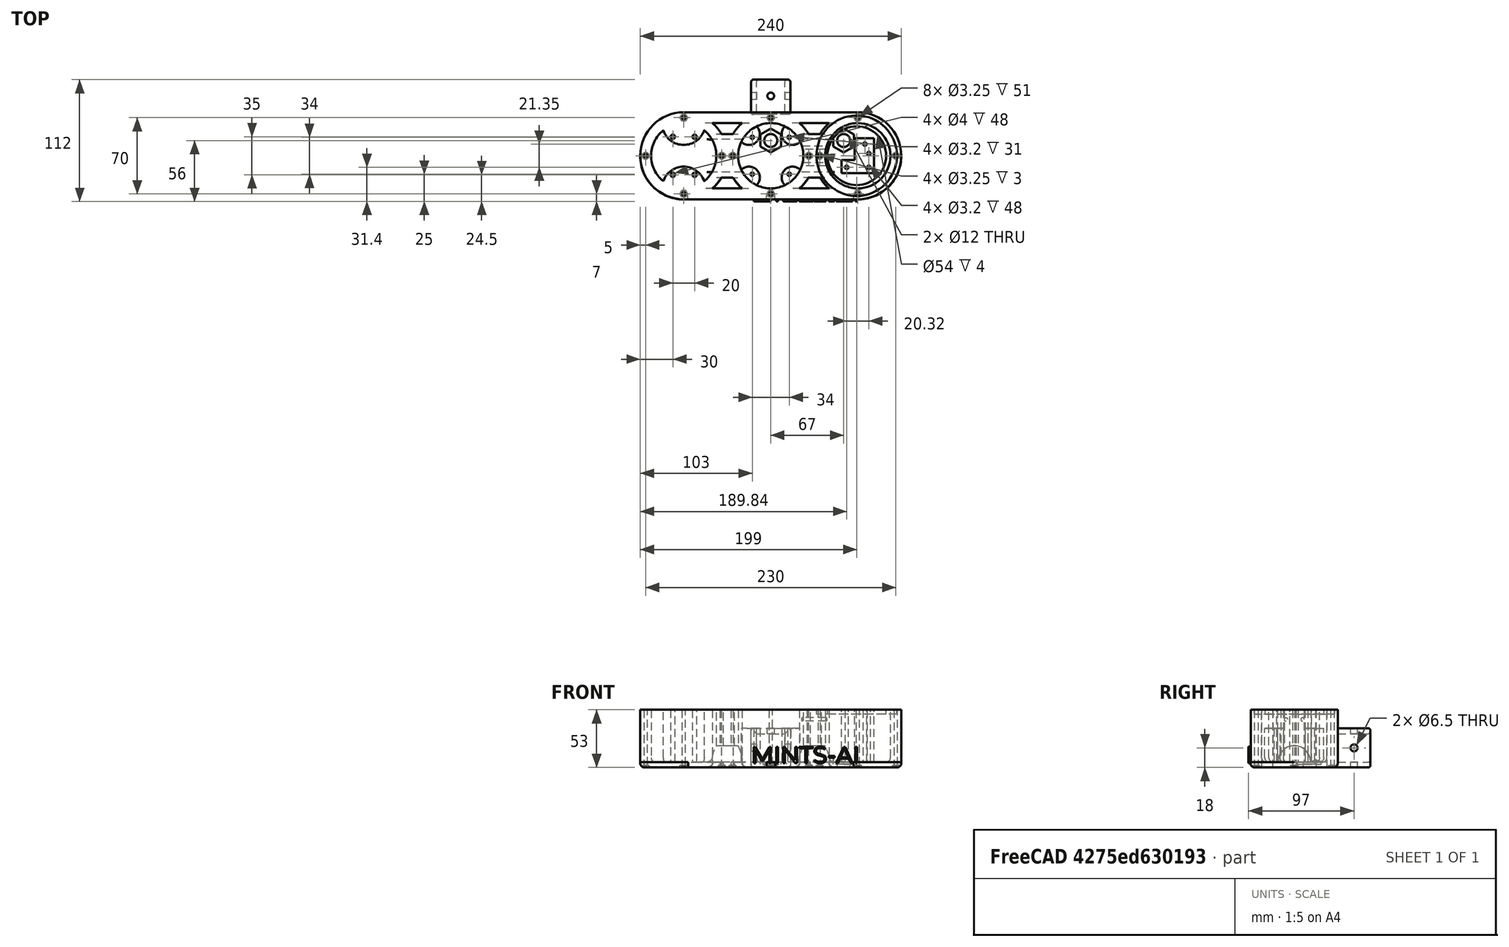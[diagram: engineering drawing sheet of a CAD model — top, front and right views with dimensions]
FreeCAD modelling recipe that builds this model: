
FCSTD DOCUMENT  (FreeCAD 1.0R39319 (Git))
Label: newLight
License: All rights reserved
LicenseURL: https://en.wikipedia.org/wiki/All_rights_reserved
objects: Part::MultiFuse×34, Part::FeaturePython×26, Part::Extrusion×18, Sketcher::SketchObject×17, Part::Cylinder×13, Part::Fillet×6, Part::Cut×3, Part::Part2DObjectPython×1
note: 135 computed .brp shape members not serialized (recipe doc carries the construction recipe); baked Part::Feature solids carry a one-line shape summary decoded from their .brp

FEATURE [Part::FeaturePython] Clone054  label="M3Nut076"  # WARN: FeaturePython — macro-defined, semantics opaque (R4)
  AttacherType = Attacher::AttachEngine3D
  Fuse = false
  Placement = pos=(0,0,4.5) rot=(0,0,1;0rad)
  Scale = (1.1,1.1,5)
FEATURE [Part::FeaturePython] Clone055  label="M3Nut077"  # WARN: FeaturePython — macro-defined, semantics opaque (R4)
  AttacherType = Attacher::AttachEngine3D
  Fuse = false
  Placement = pos=(0,0,0.9) rot=(0,0,1;0rad)
  Scale = (1.1,1.1,1)
FEATURE [Part::FeaturePython] Clone056  label="M3Nut078"  # WARN: FeaturePython — macro-defined, semantics opaque (R4)
  AttacherType = Attacher::AttachEngine3D
  Fuse = false
  Placement = pos=(0,0,4.5) rot=(0,0,1;0rad)
  Scale = (1.1,1.1,5)
FEATURE [Part::FeaturePython] Clone057  label="M3Nut079"  # WARN: FeaturePython — macro-defined, semantics opaque (R4)
  AttacherType = Attacher::AttachEngine3D
  Fuse = false
  Placement = pos=(0,0,0.9) rot=(0,0,1;0rad)
  Scale = (1.1,1.1,1)
FEATURE [Part::FeaturePython] Clone058  label="M3Nut080"  # WARN: FeaturePython — macro-defined, semantics opaque (R4)
  AttacherType = Attacher::AttachEngine3D
  Fuse = false
  Placement = pos=(0,0,4.5) rot=(0,0,1;0rad)
  Scale = (1.1,1.1,5)
FEATURE [Part::FeaturePython] Clone059  label="M3Nut081"  # WARN: FeaturePython — macro-defined, semantics opaque (R4)
  AttacherType = Attacher::AttachEngine3D
  Fuse = false
  Placement = pos=(0,0,0.9) rot=(0,0,1;0rad)
  Scale = (1.1,1.1,1)
FEATURE [Part::FeaturePython] Clone060  label="M3Nut082"  # WARN: FeaturePython — macro-defined, semantics opaque (R4)
  AttacherType = Attacher::AttachEngine3D
  Fuse = false
  Placement = pos=(0,0,4.5) rot=(0,0,1;0rad)
  Scale = (1.1,1.1,5)
FEATURE [Part::FeaturePython] Clone061  label="M3Nut083"  # WARN: FeaturePython — macro-defined, semantics opaque (R4)
  AttacherType = Attacher::AttachEngine3D
  Fuse = false
  Placement = pos=(0,0,0.9) rot=(0,0,1;0rad)
  Scale = (1.1,1.1,1)
FEATURE [Part::FeaturePython] Clone062  label="M3Nut084"  # WARN: FeaturePython — macro-defined, semantics opaque (R4)
  AttacherType = Attacher::AttachEngine3D
  Fuse = false
  Placement = pos=(0,0,4.5) rot=(0,0,1;0rad)
  Scale = (1.1,1.1,5)
FEATURE [Part::FeaturePython] Clone063  label="M3Nut085"  # WARN: FeaturePython — macro-defined, semantics opaque (R4)
  AttacherType = Attacher::AttachEngine3D
  Fuse = false
  Placement = pos=(0,0,0.9) rot=(0,0,1;0rad)
  Scale = (1.1,1.1,1)
FEATURE [Part::FeaturePython] Clone064  label="M3Nut086"  # WARN: FeaturePython — macro-defined, semantics opaque (R4)
  AttacherType = Attacher::AttachEngine3D
  Fuse = false
  Placement = pos=(0,0,4.5) rot=(0,0,1;0rad)
  Scale = (1.1,1.1,5)
FEATURE [Part::FeaturePython] Clone065  label="M3Nut087"  # WARN: FeaturePython — macro-defined, semantics opaque (R4)
  AttacherType = Attacher::AttachEngine3D
  Fuse = false
  Placement = pos=(0,0,0.9) rot=(0,0,1;0rad)
  Scale = (1.1,1.1,1)
FEATURE [Part::FeaturePython] Clone066  label="M3Nut088"  # WARN: FeaturePython — macro-defined, semantics opaque (R4)
  AttacherType = Attacher::AttachEngine3D
  Fuse = false
  Placement = pos=(0,0,4.5) rot=(0,0,1;0rad)
  Scale = (1.1,1.1,5)
FEATURE [Part::FeaturePython] Clone067  label="M3Nut089"  # WARN: FeaturePython — macro-defined, semantics opaque (R4)
  AttacherType = Attacher::AttachEngine3D
  Fuse = false
  Placement = pos=(0,0,0.9) rot=(0,0,1;0rad)
  Scale = (1.1,1.1,1)
FEATURE [Part::FeaturePython] Clone068  label="M3Nut090"  # WARN: FeaturePython — macro-defined, semantics opaque (R4)
  AttacherType = Attacher::AttachEngine3D
  Fuse = false
  Placement = pos=(0,0,4.5) rot=(0,0,1;0rad)
  Scale = (1.1,1.1,5)
FEATURE [Part::FeaturePython] Clone069  label="M3Nut091"  # WARN: FeaturePython — macro-defined, semantics opaque (R4)
  AttacherType = Attacher::AttachEngine3D
  Fuse = false
  Placement = pos=(0,0,0.9) rot=(0,0,1;0rad)
  Scale = (1.1,1.1,1)
FEATURE [Part::FeaturePython] Clone070  label="M3Nut092"  # WARN: FeaturePython — macro-defined, semantics opaque (R4)
  AttacherType = Attacher::AttachEngine3D
  Fuse = false
  Placement = pos=(0,0,4.5) rot=(0,0,1;0rad)
  Scale = (1.1,1.1,5)
FEATURE [Part::FeaturePython] Clone071  label="M3Nut093"  # WARN: FeaturePython — macro-defined, semantics opaque (R4)
  AttacherType = Attacher::AttachEngine3D
  Fuse = false
  Placement = pos=(0,0,0.9) rot=(0,0,1;0rad)
  Scale = (1.1,1.1,1)
FEATURE [Part::FeaturePython] Clone072  label="M3Nut094"  # WARN: FeaturePython — macro-defined, semantics opaque (R4)
  AttacherType = Attacher::AttachEngine3D
  Fuse = false
  Placement = pos=(0,0,4.5) rot=(0,0,1;0rad)
  Scale = (1.1,1.1,5)
FEATURE [Part::FeaturePython] Clone073  label="M3Nut095"  # WARN: FeaturePython — macro-defined, semantics opaque (R4)
  AttacherType = Attacher::AttachEngine3D
  Fuse = false
  Placement = pos=(0,0,0.9) rot=(0,0,1;0rad)
  Scale = (1.1,1.1,1)
FEATURE [Part::FeaturePython] Clone074  label="M3Nut096"  # WARN: FeaturePython — macro-defined, semantics opaque (R4)
  AttacherType = Attacher::AttachEngine3D
  Fuse = false
  Placement = pos=(0,0,4.5) rot=(0,0,1;0rad)
  Scale = (1.1,1.1,5)
FEATURE [Part::FeaturePython] Clone075  label="M3Nut097"  # WARN: FeaturePython — macro-defined, semantics opaque (R4)
  AttacherType = Attacher::AttachEngine3D
  Fuse = false
  Placement = pos=(0,0,0.9) rot=(0,0,1;0rad)
  Scale = (1.1,1.1,1)
FEATURE [Part::FeaturePython] Clone076  label="M3Nut098"  # WARN: FeaturePython — macro-defined, semantics opaque (R4)
  AttacherType = Attacher::AttachEngine3D
  Fuse = false
  Placement = pos=(0,0,4.5) rot=(0,0,1;0rad)
  Scale = (1.1,1.1,5)
FEATURE [Part::FeaturePython] Clone077  label="M3Nut099"  # WARN: FeaturePython — macro-defined, semantics opaque (R4)
  AttacherType = Attacher::AttachEngine3D
  Fuse = false
  Placement = pos=(0,0,0.9) rot=(0,0,1;0rad)
  Scale = (1.1,1.1,1)
FEATURE [Part::FeaturePython] Clone078  label="M3Nut100"  # WARN: FeaturePython — macro-defined, semantics opaque (R4)
  AttacherType = Attacher::AttachEngine3D
  Fuse = false
  Placement = pos=(0,0,4.5) rot=(0,0,1;0rad)
  Scale = (1.1,1.1,5)
FEATURE [Part::FeaturePython] Clone079  label="M3Nut101"  # WARN: FeaturePython — macro-defined, semantics opaque (R4)
  AttacherType = Attacher::AttachEngine3D
  Fuse = false
  Placement = pos=(0,0,0.9) rot=(0,0,1;0rad)
  Scale = (1.1,1.1,1)
FEATURE [Part::Cylinder] Cylinder207 .. Cylinder219  x13 (patterned run collapsed; names and placements below)
  Angle = 360
  AttacherType = Attacher::AttachEngine3D
  FirstAngle = 0
  Height = 9
  Radius = 2
  SecondAngle = 0
FEATURE [Part::MultiFuse] Fusion265
  Shapes = -> [Clone054,Cylinder207]
FEATURE [Part::MultiFuse] Fusion266  label="m3NutCut027"
  Placement = pos=(-80,-235,-22.5) rot=(0.707107,-0.707107,0;3.14159rad)
  Shapes = -> [Clone055,Fusion265]
FEATURE [Part::MultiFuse] Fusion267
  Shapes = -> [Clone056,Cylinder208]
FEATURE [Part::MultiFuse] Fusion268  label="m3NutCut028"
  Placement = pos=(-115,-270,-22.5) rot=(1,0,0;3.14159rad)
  Shapes = -> [Clone057,Fusion267]
FEATURE [Part::MultiFuse] Fusion269
  Shapes = -> [Clone058,Cylinder209]
FEATURE [Part::MultiFuse] Fusion270  label="m3NutCut029"
  Placement = pos=(-45,-270,-22.5) rot=(1,0,0;3.14159rad)
  Shapes = -> [Clone059,Fusion269]
FEATURE [Part::MultiFuse] Fusion271
  Shapes = -> [Clone060,Cylinder210]
FEATURE [Part::MultiFuse] Fusion272  label="m3NutCut030"
  Placement = pos=(-35,-270,-22.5) rot=(1,0,0;3.14159rad)
  Shapes = -> [Clone061,Fusion271]
FEATURE [Part::MultiFuse] Fusion273
  Shapes = -> [Clone062,Cylinder211]
FEATURE [Part::MultiFuse] Fusion274  label="m3NutCut031"
  Placement = pos=(35,-270,-22.5) rot=(1,0,0;3.14159rad)
  Shapes = -> [Clone063,Fusion273]
FEATURE [Part::MultiFuse] Fusion275
  Shapes = -> [Clone064,Cylinder212]
FEATURE [Part::MultiFuse] Fusion276  label="m3NutCut032"
  Placement = pos=(45,-270,-22.5) rot=(1,0,0;3.14159rad)
  Shapes = -> [Clone065,Fusion275]
FEATURE [Part::MultiFuse] Fusion277
  Shapes = -> [Clone066,Cylinder213]
FEATURE [Part::MultiFuse] Fusion278  label="m3NutCut033"
  Placement = pos=(115,-270,-22.5) rot=(1,0,0;3.14159rad)
  Shapes = -> [Clone067,Fusion277]
FEATURE [Part::MultiFuse] Fusion279
  Shapes = -> [Clone068,Cylinder214]
FEATURE [Part::MultiFuse] Fusion280  label="m3NutCut034"
  Placement = pos=(-80,-235,-22.5) rot=(0.707107,-0.707107,0;3.14159rad)
  Shapes = -> [Clone069,Fusion279]
FEATURE [Part::MultiFuse] Fusion281
  Shapes = -> [Clone070,Cylinder215]
FEATURE [Part::MultiFuse] Fusion282  label="m3NutCut035"
  Placement = pos=(0,-235,-22.5) rot=(0.707107,-0.707107,0;3.14159rad)
  Shapes = -> [Clone071,Fusion281]
FEATURE [Part::MultiFuse] Fusion283
  Shapes = -> [Clone072,Cylinder216]
FEATURE [Part::MultiFuse] Fusion284  label="m3NutCut036"
  Placement = pos=(80,-235,-22.5) rot=(0.707107,-0.707107,0;3.14159rad)
  Shapes = -> [Clone073,Fusion283]
FEATURE [Part::MultiFuse] Fusion285
  Shapes = -> [Clone074,Cylinder217]
FEATURE [Part::MultiFuse] Fusion286  label="m3NutCut037"
  Placement = pos=(80,-305,-22.5) rot=(0.707107,-0.707107,0;3.14159rad)
  Shapes = -> [Clone075,Fusion285]
FEATURE [Part::MultiFuse] Fusion287
  Shapes = -> [Clone076,Cylinder218]
FEATURE [Part::MultiFuse] Fusion288  label="m3NutCut038"
  Placement = pos=(1.4e-14,-305,-22.5) rot=(0.707107,-0.707107,0;3.14159rad)
  Shapes = -> [Clone077,Fusion287]
FEATURE [Part::MultiFuse] Fusion289
  Shapes = -> [Clone078,Cylinder219]
FEATURE [Part::MultiFuse] Fusion290  label="m3NutCut039"
  Placement = pos=(-80,-305,-22.5) rot=(0.707107,-0.707107,0;3.14159rad)
  Shapes = -> [Clone079,Fusion289]
FEATURE [Part::MultiFuse] Fusion291  label="m3NutCuts001"
  Placement = pos=(0,0,-0.5) rot=(0,0,1;0rad)
  Shapes = -> [Fusion266,Fusion268,Fusion270,Fusion272,Fusion274,Fusion276,Fusion278,Fusion280,Fusion282,Fusion284,Fusion286,Fusion288,Fusion290]
FEATURE [Part::Part2DObjectPython] ShapeString002  # Draft 2D object (typed FeaturePython)
  FontFile = <userpath>/Downloads/Montserrat-Regular.otf
  Fuse = false
  Justification = 6
  JustificationReference = 0
  KeepLeftMargin = false
  MakeFace = true
  ObliqueAngle = 0
  Placement = pos=(-15.5,-310,-21) rot=(1,0,0;1.5708rad)
  ScaleToSize = true
  Size = 15
  String = MINTS-AI
  Tracking = 0
FEATURE [Part::Extrusion] Extrude191  label="text001"
  Base = -> ShapeString002
  Dir = (0,-1,2e-16)
  DirMode = 2
  FaceMakerClass = Part::FaceMakerBullseye
  FaceMakerMode = 3
  LengthFwd = 2
  LengthRev = 0
  Solid = false
  Symmetric = false
FEATURE [Sketcher::SketchObject] Sketch409
  ArcFitTolerance = 0
  FullyConstrained = true
  MakeInternals = false
  Placement = pos=(0,0,-25) rot=(0,0,1;0rad)
  sketch-geometry (12):
    g0: Circle CenterX=-115 CenterY=-270 CenterZ=0 NormalX=0 NormalY=0 NormalZ=1 AngleXU=0 Radius=1.625
    g1: Circle CenterX=-80 CenterY=-235 CenterZ=0 NormalX=0 NormalY=0 NormalZ=1 AngleXU=0 Radius=1.625
    g2: Circle CenterX=-80 CenterY=-305 CenterZ=0 NormalX=0 NormalY=0 NormalZ=1 AngleXU=0 Radius=1.625
    g3: Circle CenterX=-45 CenterY=-270 CenterZ=0 NormalX=0 NormalY=0 NormalZ=1 AngleXU=0 Radius=1.625
    g4: Circle CenterX=-35 CenterY=-270 CenterZ=0 NormalX=0 NormalY=0 NormalZ=1 AngleXU=0 Radius=1.625
    g5: Circle CenterX=0 CenterY=-305 CenterZ=0 NormalX=0 NormalY=0 NormalZ=1 AngleXU=0 Radius=1.625
    g6: Circle CenterX=0 CenterY=-235 CenterZ=0 NormalX=0 NormalY=0 NormalZ=1 AngleXU=0 Radius=1.625
    g7: Circle CenterX=35 CenterY=-270 CenterZ=0 NormalX=0 NormalY=0 NormalZ=1 AngleXU=0 Radius=1.625
    g8: Circle CenterX=45 CenterY=-270 CenterZ=0 NormalX=0 NormalY=0 NormalZ=1 AngleXU=0 Radius=1.625
    g9: Circle CenterX=80 CenterY=-235 CenterZ=0 NormalX=0 NormalY=0 NormalZ=1 AngleXU=0 Radius=1.625
    g10: Circle CenterX=115 CenterY=-270 CenterZ=0 NormalX=0 NormalY=0 NormalZ=1 AngleXU=0 Radius=1.625
    g11: Circle CenterX=80 CenterY=-305 CenterZ=0 NormalX=0 NormalY=0 NormalZ=1 AngleXU=0 Radius=1.625
  constraints (36):
    c: PointOnObject(g5,g-2)
    c: PointOnObject(g6,g-2)
    c: Equal(g8,g1)
    c: Equal(g8,g6)
    c: Equal(g8,g9)
    c: Equal(g8,g2)
    c: Equal(g8,g5)
    c: Equal(g8,g11)
    c: Equal(g8,g0)
    c: Equal(g8,g3)
    c: Equal(g8,g4)
    c: Equal(g8,g7)
    c: Equal(g8,g10)
    c: Diameter(g8) = 3.25
    c: Horizontal(g0,g3)
    c: Horizontal(g3,g4)
    c: Horizontal(g4,g7)
    c: Horizontal(g7,g8)
    c: Horizontal(g8,g10)
    c: Horizontal(g2,g5)
    c: Horizontal(g5,g11)
    c: Horizontal(g6,g9)
    c: Horizontal(g1,g6)
    c: Vertical(g2,g1)
    c: Vertical(g9,g11)
    c: DistanceY(g0) = -270
    c: DistanceX(g0) = -115
    c: DistanceX(g0,g2) = 35
    c: DistanceY(g2,g0) = 35
    c: DistanceY(g0,g1) = 35
    c: DistanceX(g0,g3) = 70
    c: DistanceX(g4) = -35
    c: DistanceX(g7) = 35
    c: DistanceX(g8) = 45
    c: DistanceX(g8,g10) = 70
    c: DistanceX(g8,g11) = 35
FEATURE [Part::Extrusion] Extrude184  label="m3Cuts001"
  Base = -> Sketch409
  Dir = (0,0,1)
  DirMode = 2
  FaceMakerClass = Part::FaceMakerBullseye
  FaceMakerMode = 3
  LengthFwd = 60
  LengthRev = 0
  Solid = true
  Symmetric = false
FEATURE [Sketcher::SketchObject] Sketch410
  ArcFitTolerance = 0
  FullyConstrained = true
  MakeInternals = false
  Placement = pos=(24,0,0) rot=(0.57735,0.57735,0.57735;2.0944rad)
  sketch-geometry (2):
    g0: Circle CenterX=-277.6 CenterY=19.15 CenterZ=0 NormalX=0 NormalY=0 NormalZ=1 AngleXU=0 Radius=1.6
    g1: Circle CenterX=-262.4 CenterY=19.15 CenterZ=0 NormalX=0 NormalY=0 NormalZ=1 AngleXU=0 Radius=1.6
  constraints (6):
    c: Horizontal(g1,g0)
    c: Equal(g1,g0)
    c: Diameter(g1) = 3.2
    c: DistanceX(g0) = -277.6
    c: DistanceY(g0) = 19.15
    c: DistanceX(g0,g1) = 15.2
FEATURE [Part::Extrusion] Extrude185
  Base = -> Sketch410
  Dir = (1,0,0)
  DirMode = 2
  FaceMakerClass = Part::FaceMakerBullseye
  FaceMakerMode = 3
  LengthFwd = 30
  LengthRev = 0
  Solid = true
  Symmetric = false
FEATURE [Sketcher::SketchObject] Sketch411
  ArcFitTolerance = 0
  FullyConstrained = true
  MakeInternals = false
  Placement = pos=(0,0,-22) rot=(0,0,1;0rad)
  sketch-geometry (14):
    g0: LineSegment StartX=-2e-16 StartY=-267 StartZ=0 EndX=9.52628 EndY=-261.5 EndZ=0
    g1: LineSegment StartX=9.52628 StartY=-261.5 StartZ=0 EndX=9.52628 EndY=-250.5 EndZ=0
    g2: LineSegment StartX=9.52628 StartY=-250.5 StartZ=0 EndX=2e-16 EndY=-245 EndZ=0
    g3: LineSegment StartX=2e-16 StartY=-245 StartZ=0 EndX=-9.52628 EndY=-250.5 EndZ=0
    g4: LineSegment StartX=-9.52628 StartY=-250.5 StartZ=0 EndX=-9.52628 EndY=-261.5 EndZ=0
    g5: LineSegment StartX=-9.52628 StartY=-261.5 StartZ=0 EndX=-2e-16 EndY=-267 EndZ=0
    g6: Circle [constr] CenterX=2e-16 CenterY=-256 CenterZ=0 NormalX=0 NormalY=0 NormalZ=1 AngleXU=0 Radius=11
    g7: LineSegment StartX=67 StartY=-267 StartZ=0 EndX=76.5263 EndY=-261.5 EndZ=0
    g8: LineSegment StartX=76.5263 StartY=-261.5 StartZ=0 EndX=76.5263 EndY=-250.5 EndZ=0
    g9: LineSegment StartX=76.5263 StartY=-250.5 StartZ=0 EndX=67 EndY=-245 EndZ=0
    g10: LineSegment StartX=67 StartY=-245 StartZ=0 EndX=57.4737 EndY=-250.5 EndZ=0
    g11: LineSegment StartX=57.4737 StartY=-250.5 StartZ=0 EndX=57.4737 EndY=-261.5 EndZ=0
    g12: LineSegment StartX=57.4737 StartY=-261.5 StartZ=0 EndX=67 EndY=-267 EndZ=0
    g13: Circle [constr] CenterX=67 CenterY=-256 CenterZ=0 NormalX=0 NormalY=0 NormalZ=1 AngleXU=0 Radius=11
  constraints (34):
    c: Coincident(g0,g1)
    c: Coincident(g1,g2)
    c: Coincident(g2,g3)
    c: Coincident(g3,g4)
    c: Coincident(g4,g5)
    c: Coincident(g5,g0)
    c: Equal(g0, g1-g5) x5
    c: PointOnObject(g0,g6)
    c: PointOnObject(g1,g6)
    c: PointOnObject(g2,g6)
    c: PointOnObject(g3,g6)
    c: PointOnObject(g4,g6)
    c: PointOnObject(g5,g6)
    c: Coincident(g7,g8)
    c: Coincident(g8,g9)
    c: Coincident(g9,g10)
    c: Coincident(g10,g11)
    c: Coincident(g11,g12)
    c: Coincident(g12,g7)
    c: Equal(g7, g8-g12) x5
    c: PointOnObject(g7,g13)
    c: PointOnObject(g8,g13)
    c: PointOnObject(g9,g13)
    c: PointOnObject(g10,g13)
    c: PointOnObject(g11,g13)
    c: PointOnObject(g12,g13)
    c: Horizontal(g6,g13)
    c: Vertical(g6,g2)
    c: DistanceX(g6) = 0
    c: DistanceY(g6) = -256
    c: Diameter(g6) = 22
    c: Vertical(g13,g7)
    c: Diameter(g13) = 22
    c: DistanceX(g13) = 67
FEATURE [Part::Extrusion] Extrude186
  Base = -> Sketch411
  Dir = (0,0,1)
  DirMode = 2
  FaceMakerClass = Part::FaceMakerBullseye
  FaceMakerMode = 3
  LengthFwd = 6
  LengthRev = 0
  Solid = true
  Symmetric = false
FEATURE [Part::MultiFuse] Fusion293  label="pg7Cuts001"
  Shapes = -> [Extrude185,Extrude186]
FEATURE [Sketcher::SketchObject] Sketch412
  ArcFitTolerance = 0
  FullyConstrained = true
  MakeInternals = false
  Placement = pos=(0,-232,0) rot=(1,0,0;1.5708rad)
  sketch-geometry (8):
    g0: LineSegment StartX=-13 StartY=6 StartZ=0 EndX=13 EndY=6 EndZ=0
    g1: LineSegment StartX=13 StartY=6 StartZ=0 EndX=13 EndY=-20 EndZ=0
    g2: LineSegment StartX=13 StartY=-20 StartZ=0 EndX=-13 EndY=-20 EndZ=0
    g3: LineSegment StartX=-13 StartY=-20 StartZ=0 EndX=-13 EndY=6 EndZ=0
    g4: LineSegment StartX=-18 StartY=11 StartZ=0 EndX=18 EndY=11 EndZ=0
    g5: LineSegment StartX=18 StartY=11 StartZ=0 EndX=18 EndY=-25 EndZ=0
    g6: LineSegment StartX=18 StartY=-25 StartZ=0 EndX=-18 EndY=-25 EndZ=0
    g7: LineSegment StartX=-18 StartY=-25 StartZ=0 EndX=-18 EndY=11 EndZ=0
  constraints (24):
    c: Coincident(g0,g1)
    c: Coincident(g1,g2)
    c: Coincident(g2,g3)
    c: Coincident(g3,g0)
    c: Horizontal(g0)
    c: Horizontal(g2)
    c: Vertical(g1)
    c: Vertical(g3)
    c: Coincident(g4,g5)
    c: Coincident(g5,g6)
    c: Coincident(g6,g7)
    c: Coincident(g7,g4)
    c: Horizontal(g4)
    c: Horizontal(g6)
    c: Vertical(g5)
    c: Vertical(g7)
    c: DistanceY(g6) = -25
    c: DistanceX(g2,g1) = 26
    c: DistanceX(g6) = -18
    c: DistanceX(g6,g2) = 5
    c: DistanceX(g5) = 18
    c: DistanceY(g2,g0) = 26
    c: DistanceY(g6,g2) = 5
    c: DistanceY(g0,g4) = 5
FEATURE [Part::Extrusion] Extrude187
  Base = -> Sketch412
  Dir = (0,-1,2e-16)
  DirMode = 2
  FaceMakerClass = Part::FaceMakerBullseye
  FaceMakerMode = 3
  LengthFwd = 32
  LengthRev = 0
  Reversed = true
  Solid = true
  Symmetric = false
FEATURE [Sketcher::SketchObject] Sketch413
  ArcFitTolerance = 0
  FullyConstrained = true
  MakeInternals = false
  Placement = pos=(0,0,11) rot=(0,0,1;0rad)
  sketch-geometry (1):
    g0: Circle CenterX=0 CenterY=-215 CenterZ=0 NormalX=0 NormalY=0 NormalZ=1 AngleXU=0 Radius=3.125
  constraints (3):
    c: DistanceX(g0) = 0
    c: DistanceY(g0) = -215
    c: Diameter(g0) = 6.25
FEATURE [Part::Extrusion] Extrude189
  Base = -> Sketch413
  Dir = (0,0,1)
  DirMode = 2
  FaceMakerClass = Part::FaceMakerBullseye
  FaceMakerMode = 3
  LengthFwd = 36
  LengthRev = 0
  Reversed = true
  Solid = true
  Symmetric = false
FEATURE [Sketcher::SketchObject] Sketch414
  ArcFitTolerance = 0
  FullyConstrained = true
  MakeInternals = false
  Placement = pos=(-18,0,0) rot=(0.57735,0.57735,0.57735;2.0944rad)
  sketch-geometry (1):
    g0: Circle CenterX=-215 CenterY=-7 CenterZ=0 NormalX=0 NormalY=0 NormalZ=1 AngleXU=0 Radius=3.25
  constraints (3):
    c: DistanceX(g0) = -215
    c: DistanceY(g0) = -7
    c: Diameter(g0) = 6.5
FEATURE [Part::Extrusion] Extrude188
  Base = -> Sketch414
  Dir = (1,0,0)
  DirMode = 2
  FaceMakerClass = Part::FaceMakerBullseye
  FaceMakerMode = 3
  LengthFwd = 36
  LengthRev = 0
  Solid = true
  Symmetric = false
FEATURE [Part::MultiFuse] Fusion292
  Shapes = -> [Extrude189,Extrude188]
FEATURE [Part::Cut] Cut158  label="in004"
  Base = -> Extrude187
  Tool = -> Fusion292
FEATURE [Part::Fillet] Fillet262
  Base = -> Cut158
  EdgeLinks = -> Cut158 [?Edge1,?Edge4,?Edge6,?Edge22]
  Edges = 4 edges r=2: [Edge1,Edge4,Edge6,Edge22]
FEATURE [Part::Fillet] Fillet263  label="tSlotHolder001"
  Base = -> Fillet262
  EdgeLinks = -> Fillet262 [Edge4,Edge18,Edge20,Edge21,Edge22,Edge23,Edge24,Edge25,Edge26,Edge27,Edge28,Edge29]
  Edges = 12 edges r=2: [Edge4,Edge18,Edge20,Edge21,Edge22,Edge23,Edge24,Edge25,Edge26,Edge27,Edge28,Edge29]
FEATURE [Sketcher::SketchObject] Sketch415
  ArcFitTolerance = 0
  FullyConstrained = true
  MakeInternals = false
  Placement = pos=(0,0,-25) rot=(0,0,1;0rad)
  sketch-geometry (2):
    g0: Circle CenterX=0 CenterY=-256 CenterZ=0 NormalX=0 NormalY=0 NormalZ=1 AngleXU=0 Radius=6
    g1: Circle CenterX=67 CenterY=-256 CenterZ=0 NormalX=0 NormalY=0 NormalZ=1 AngleXU=0 Radius=6
  constraints (6):
    c: DistanceY(g0) = -256
    c: Horizontal(g0,g1)
    c: DistanceX(g0,g1) = 67
    c: DistanceX(g0) = 0
    c: Equal(g0,g1)
    c: Diameter(g0) = 12
FEATURE [Part::Extrusion] Extrude190  label="outCut001"
  Base = -> Sketch415
  Dir = (0,0,1)
  DirMode = 2
  FaceMakerClass = Part::FaceMakerBullseye
  FaceMakerMode = 3
  LengthFwd = 5
  LengthRev = 0
  Solid = true
  Symmetric = false
FEATURE [Part::MultiFuse] Fusion297  label="mainCuts001"
  Shapes = -> [Fusion293,Fusion291,Extrude190,Extrude184]
FEATURE [Sketcher::SketchObject] Sketch416
  ArcFitTolerance = 0
  FullyConstrained = true
  MakeInternals = false
  Placement = pos=(0,0,-25) rot=(0,0,1;0rad)
  sketch-geometry (8):
    g0: ArcOfCircle CenterX=-80 CenterY=-270 CenterZ=0 NormalX=0 NormalY=0 NormalZ=1 AngleXU=0 Radius=40 StartAngle=1.5708 EndAngle=4.71239
    g1: ArcOfCircle CenterX=80 CenterY=-270 CenterZ=0 NormalX=0 NormalY=0 NormalZ=1 AngleXU=0 Radius=40 StartAngle=4.71239 EndAngle=7.85398
    g2: LineSegment StartX=-80 StartY=-310 StartZ=0 EndX=80 EndY=-310 EndZ=0
    g3: LineSegment StartX=80 StartY=-230 StartZ=0 EndX=-80 EndY=-230 EndZ=0
    g4: ArcOfCircle CenterX=-80 CenterY=-270 CenterZ=0 NormalX=0 NormalY=0 NormalZ=1 AngleXU=0 Radius=30 StartAngle=1.5708 EndAngle=4.71239
    g5: ArcOfCircle CenterX=80 CenterY=-270 CenterZ=0 NormalX=0 NormalY=0 NormalZ=1 AngleXU=0 Radius=30 StartAngle=4.71239 EndAngle=7.85398
    g6: LineSegment StartX=-80 StartY=-300 StartZ=0 EndX=80 EndY=-300 EndZ=0
    g7: LineSegment StartX=80 StartY=-240 StartZ=0 EndX=-80 EndY=-240 EndZ=0
  constraints (18):
    c: Tangent(g0,g2) = -1.5708
    c: Tangent(g2,g1) = -1.5708
    c: Tangent(g1,g3) = -1.5708
    c: Tangent(g3,g0) = -1.5708
    c: Equal(g0,g1)
    c: Horizontal(g2)
    c: DistanceY(g0) = -270
    c: DistanceX(g0) = -80
    c: DistanceX(g1) = 80
    c: Diameter(g0) = 80
    c: Tangent(g4,g6) = -1.5708
    c: Tangent(g6,g5) = -1.5708
    c: Tangent(g5,g7) = -1.5708
    c: Tangent(g7,g4) = -1.5708
    c: Equal(g4,g5)
    c: Coincident(g4,g0)
    c: Coincident(g5,g1)
    c: Diameter(g4) = 60
FEATURE [Part::Extrusion] Extrude192  label="outerBorder002"
  Base = -> Sketch416
  Dir = (0,0,1)
  DirMode = 2
  FaceMakerClass = Part::FaceMakerBullseye
  FaceMakerMode = 3
  LengthFwd = 53
  LengthRev = 0
  Solid = true
  Symmetric = false
FEATURE [Part::Fillet] Fillet264  label="outerHold002"
  Base = -> Extrude192
  EdgeLinks = -> Extrude192 [Edge9]
  Edges = 1 edges r=4: [Edge9]
FEATURE [Sketcher::SketchObject] Sketch417
  ArcFitTolerance = 0
  FullyConstrained = true
  MakeInternals = false
  Placement = pos=(0,0,-25) rot=(0,0,1;0rad)
  sketch-geometry (8):
    g0: ArcOfCircle CenterX=-80 CenterY=-270 CenterZ=0 NormalX=0 NormalY=0 NormalZ=1 AngleXU=0 Radius=30 StartAngle=5.55346 EndAngle=7.01291
    g1: LineSegment StartX=-57.6393 StartY=-250 StartZ=0 EndX=-22.3607 EndY=-250 EndZ=0
    g2: LineSegment StartX=-57.6393 StartY=-290 StartZ=0 EndX=-22.3607 EndY=-290 EndZ=0
    g3: ArcOfCircle CenterX=0 CenterY=-270 CenterZ=0 NormalX=0 NormalY=0 NormalZ=1 AngleXU=0 Radius=30 StartAngle=2.41186 EndAngle=3.87132
    g4: ArcOfCircle CenterX=0 CenterY=-270 CenterZ=0 NormalX=0 NormalY=0 NormalZ=1 AngleXU=0 Radius=30 StartAngle=5.55346 EndAngle=7.01291
    g5: ArcOfCircle CenterX=80 CenterY=-270 CenterZ=0 NormalX=0 NormalY=0 NormalZ=1 AngleXU=0 Radius=30 StartAngle=2.41186 EndAngle=3.87132
    g6: LineSegment StartX=22.3607 StartY=-250 StartZ=0 EndX=57.6393 EndY=-250 EndZ=0
    g7: LineSegment StartX=57.6393 StartY=-290 StartZ=0 EndX=22.3607 EndY=-290 EndZ=0
  constraints (27):
    c: Coincident(g1,g0)
    c: Horizontal(g1)
    c: Coincident(g2,g0)
    c: Horizontal(g2)
    c: PointOnObject(g3,g-2)
    c: Coincident(g3,g2)
    c: Coincident(g3,g1)
    c: Coincident(g4,g3)
    c: Coincident(g6,g4)
    c: Coincident(g6,g5)
    c: Horizontal(g6)
    c: Coincident(g7,g5)
    c: Coincident(g7,g4)
    c: Horizontal(g7)
    c: Horizontal(g0,g4)
    c: Horizontal(g2,g4)
    c: Equal(g3,g0)
    c: Equal(g3,g5)
    c: Equal(g3,g4)
    c: Diameter(g3) = 60
    c: DistanceY(g3) = -270
    c: Vertical(g0,g0)
    c: Vertical(g2,g1)
    c: Vertical(g5,g5)
    c: DistanceX(g5) = 80
    c: DistanceX(g0) = -80
    c: DistanceY(g4) = -250
FEATURE [Part::Extrusion] Extrude193  label="3WayHolds002"
  Base = -> Sketch417
  Dir = (0,0,1)
  DirMode = 2
  FaceMakerClass = Part::FaceMakerBullseye
  FaceMakerMode = 3
  LengthFwd = 53
  LengthRev = 0
  Solid = true
  Symmetric = false
FEATURE [Sketcher::SketchObject] Sketch418
  ArcFitTolerance = 0
  FullyConstrained = true
  MakeInternals = false
  Placement = pos=(0,0,-20) rot=(0,0,1;0rad)
  sketch-geometry (18):
    g0: ArcOfCircle CenterX=-80 CenterY=-240 CenterZ=0 NormalX=0 NormalY=0 NormalZ=1 AngleXU=0 Radius=20 StartAngle=3.48143 EndAngle=5.94335
    g1: ArcOfCircle CenterX=-80 CenterY=-300 CenterZ=0 NormalX=0 NormalY=0 NormalZ=1 AngleXU=0 Radius=20 StartAngle=0.339837 EndAngle=2.80176
    g2: ArcOfCircle CenterX=-80 CenterY=-270 CenterZ=0 NormalX=0 NormalY=0 NormalZ=1 AngleXU=0 Radius=30 StartAngle=0.891123 EndAngle=2.25047
    g3: ArcOfCircle CenterX=-80 CenterY=-270 CenterZ=0 NormalX=0 NormalY=0 NormalZ=1 AngleXU=0 Radius=30 StartAngle=4.03272 EndAngle=5.39206
    g4: LineSegment StartX=65 StartY=-286 StartZ=0 EndX=95 EndY=-286 EndZ=0
    g5: LineSegment StartX=95 StartY=-286 StartZ=0 EndX=95 EndY=-254 EndZ=0
    g6: LineSegment StartX=95 StartY=-254 StartZ=0 EndX=77 EndY=-254 EndZ=0
    g7: LineSegment StartX=77 StartY=-254 StartZ=0 EndX=77 EndY=-274 EndZ=0
    g8: LineSegment StartX=77 StartY=-274 StartZ=0 EndX=65 EndY=-274 EndZ=0
    g9: LineSegment StartX=65 StartY=-274 StartZ=0 EndX=65 EndY=-286 EndZ=0
    g10: Circle CenterX=-90 CenterY=-252.5 CenterZ=0 NormalX=0 NormalY=0 NormalZ=1 AngleXU=0 Radius=2
    g11: Circle CenterX=-70 CenterY=-252.5 CenterZ=0 NormalX=0 NormalY=0 NormalZ=1 AngleXU=0 Radius=2
    g12: Circle CenterX=-90 CenterY=-287.5 CenterZ=0 NormalX=0 NormalY=0 NormalZ=1 AngleXU=0 Radius=2
    g13: Circle CenterX=-70 CenterY=-287.5 CenterZ=0 NormalX=0 NormalY=0 NormalZ=1 AngleXU=0 Radius=2
    g14: Circle CenterX=69.84 CenterY=-280.6 CenterZ=0 NormalX=0 NormalY=0 NormalZ=1 AngleXU=0 Radius=1.6
    g15: Circle CenterX=90.16 CenterY=-280.6 CenterZ=0 NormalX=0 NormalY=0 NormalZ=1 AngleXU=0 Radius=1.6
    g16: Circle CenterX=90.16 CenterY=-267.9 CenterZ=0 NormalX=0 NormalY=0 NormalZ=1 AngleXU=0 Radius=1.6
    g17: Circle CenterX=86.5 CenterY=-259.25 CenterZ=0 NormalX=0 NormalY=0 NormalZ=1 AngleXU=0 Radius=1.6
  constraints (57):
    c: Vertical(g0,g1)
    c: Coincident(g2,g0)
    c: Coincident(g3,g2)
    c: Coincident(g3,g1)
    c: Coincident(g0,g2)
    c: Coincident(g1,g3)
    c: DistanceX(g2) = -80
    c: DistanceY(g2) = -270
    c: Equal(g3,g2)
    c: Diameter(g3) = 60
    c: Equal(g0,g1)
    c: Diameter(g0) = 40
    c: Vertical(g0,g2)
    c: DistanceY(g0) = -240
    c: DistanceY(g1) = -300
    c: Horizontal(g4)
    c: Coincident(g5,g4)
    c: Vertical(g5)
    c: Coincident(g6,g5)
    c: Horizontal(g6)
    c: Coincident(g7,g6)
    c: Vertical(g7)
    c: Coincident(g8,g7)
    c: Horizontal(g8)
    c: Coincident(g9,g8)
    c: Coincident(g9,g4)
    c: Vertical(g9)
    c: DistanceY(g4) = -286
    c: DistanceX(g4) = 65
    c: DistanceY(g4,g8) = 12
    c: DistanceX(g4,g4) = 30
    c: DistanceX(g6,g6) = 18
    c: DistanceY(g5,g5) = 32
    c: Horizontal(g13,g12)
    c: Horizontal(g10,g11)
    c: Vertical(g12,g10)
    c: Vertical(g13,g11)
    c: DistanceX(g12,g2) = 10
    c: DistanceY(g12) = -287.5
    c: DistanceX(g12,g13) = 20
    c: DistanceY(g12,g10) = 35
    c: Equal(g10,g11)
    c: Equal(g10,g13)
    c: Equal(g10,g12)
    c: Diameter(g10) = 4
    c: Horizontal(g14,g15)
    c: Vertical(g15,g16)
    c: DistanceX(g14,g15) = 20.32
    c: DistanceY(g14) = -280.6
    c: DistanceY(g15,g16) = 12.7
    c: DistanceX(g17,g16) = 3.66
    c: DistanceY(g16,g17) = 8.65
    c: Equal(g15,g16)
    c: Equal(g15,g17)
    c: Equal(g15,g14)
    c: Diameter(g15) = 3.2
    c: DistanceX(g4,g14) = 4.84
FEATURE [Part::Extrusion] Extrude194  label="i2cHolds002"
  Base = -> Sketch418
  Dir = (0,0,1)
  DirMode = 2
  FaceMakerClass = Part::FaceMakerBullseye
  FaceMakerMode = 3
  LengthFwd = 48
  LengthRev = 0
  Solid = true
  Symmetric = false
FEATURE [Sketcher::SketchObject] Sketch419
  ArcFitTolerance = 0
  FullyConstrained = true
  MakeInternals = false
  Placement = pos=(0,0,-20) rot=(0,0,1;0rad)
  sketch-geometry (12):
    g0: ArcOfCircle CenterX=-20 CenterY=-290 CenterZ=0 NormalX=0 NormalY=0 NormalZ=1 AngleXU=0 Radius=10 StartAngle=5.49779 EndAngle=8.63938
    g1: ArcOfCircle CenterX=20 CenterY=-290 CenterZ=0 NormalX=0 NormalY=0 NormalZ=1 AngleXU=0 Radius=10 StartAngle=0.785398 EndAngle=3.92699
    g2: ArcOfCircle CenterX=20 CenterY=-250 CenterZ=0 NormalX=0 NormalY=0 NormalZ=1 AngleXU=0 Radius=10 StartAngle=2.35619 EndAngle=5.49779
    g3: ArcOfCircle CenterX=-20 CenterY=-250 CenterZ=0 NormalX=0 NormalY=0 NormalZ=1 AngleXU=0 Radius=10 StartAngle=3.92699 EndAngle=7.06858
    g4: ArcOfCircle CenterX=0 CenterY=-270 CenterZ=0 NormalX=0 NormalY=0 NormalZ=1 AngleXU=0 Radius=30 StartAngle=2.01636 EndAngle=2.69603
    g5: ArcOfCircle CenterX=0 CenterY=-270 CenterZ=0 NormalX=0 NormalY=0 NormalZ=1 AngleXU=0 Radius=30 StartAngle=0.445561 EndAngle=1.12524
    g6: ArcOfCircle CenterX=0 CenterY=-270 CenterZ=0 NormalX=0 NormalY=0 NormalZ=1 AngleXU=0 Radius=30 StartAngle=5.15795 EndAngle=5.83762
    g7: ArcOfCircle CenterX=0 CenterY=-270 CenterZ=0 NormalX=0 NormalY=0 NormalZ=1 AngleXU=0 Radius=30 StartAngle=3.58715 EndAngle=4.26683
    g8: Circle CenterX=-17 CenterY=-253 CenterZ=0 NormalX=0 NormalY=0 NormalZ=1 AngleXU=0 Radius=1.6
    g9: Circle CenterX=17 CenterY=-253 CenterZ=0 NormalX=0 NormalY=0 NormalZ=1 AngleXU=0 Radius=1.6
    g10: Circle CenterX=17 CenterY=-287 CenterZ=0 NormalX=0 NormalY=0 NormalZ=1 AngleXU=0 Radius=1.6
    g11: Circle CenterX=-17 CenterY=-287 CenterZ=0 NormalX=0 NormalY=0 NormalZ=1 AngleXU=0 Radius=1.6
  constraints (41):
    c: Vertical(g0,g3)
    c: Vertical(g1,g2)
    c: Horizontal(g2,g3)
    c: Horizontal(g1,g0)
    c: Equal(g2,g3)
    c: Equal(g2,g0)
    c: Equal(g2,g1)
    c: Diameter(g2) = 20
    c: Horizontal(g0,g1)
    c: Horizontal(g1,g0)
    c: Angle(g0) = 3.14159
    c: Vertical(g0,g3)
    c: Vertical(g0,g3)
    c: Angle(g2) = 3.14159
    c: DistanceY(g0) = -290
    c: Coincident(g4,g3)
    c: Coincident(g4,g3)
    c: Coincident(g5,g4)
    c: Coincident(g5,g2)
    c: Coincident(g5,g2)
    c: Coincident(g6,g4)
    c: Coincident(g6,g1)
    c: Coincident(g6,g1)
    c: Coincident(g7,g4)
    c: Coincident(g7,g0)
    c: Coincident(g7,g0)
    c: DistanceX(g4) = 0
    c: DistanceY(g4) = -270
    c: DistanceX(g0,g4) = 20
    c: DistanceX(g11,g4) = 17
    c: DistanceY(g11,g4) = 17
    c: DistanceX(g4,g10) = 17
    c: DistanceY(g10,g4) = 17
    c: DistanceX(g4,g9) = 17
    c: Vertical(g8,g11)
    c: Horizontal(g8,g9)
    c: DistanceY(g4,g8) = 17
    c: Equal(g10,g9)
    c: Equal(g10,g8)
    c: Equal(g10,g11)
    c: Diameter(g10) = 3.2
FEATURE [Part::Extrusion] Extrude195  label="cameraHold002"
  Base = -> Sketch419
  Dir = (0,0,1)
  DirMode = 2
  FaceMakerClass = Part::FaceMakerBullseye
  FaceMakerMode = 3
  LengthFwd = 31
  LengthRev = 0
  Solid = true
  Symmetric = false
FEATURE [Sketcher::SketchObject] Sketch420
  ArcFitTolerance = 0
  FullyConstrained = true
  MakeInternals = false
  Placement = pos=(85,0,0) rot=(0.57735,0.57735,0.57735;2.0944rad)
  sketch-geometry (2):
    g0: ArcOfCircle CenterX=-270 CenterY=-20 CenterZ=0 NormalX=0 NormalY=0 NormalZ=1 AngleXU=0 Radius=15 StartAngle=0 EndAngle=3.14159
    g1: LineSegment StartX=-285 StartY=-20 StartZ=0 EndX=-255 EndY=-20 EndZ=0
  constraints (7):
    c: Horizontal(g0,g0)
    c: Horizontal(g0,g0)
    c: DistanceX(g0) = -270
    c: DistanceY(g0) = -20
    c: Diameter(g0) = 30
    c: Coincident(g1,g0)
    c: Coincident(g1,g0)
FEATURE [Part::Extrusion] Extrude196  label="WireCutcut004"
  Base = -> Sketch420
  Dir = (1,0,0)
  DirMode = 2
  FaceMakerClass = Part::FaceMakerBullseye
  FaceMakerMode = 3
  LengthFwd = 170
  LengthRev = 0
  Reversed = true
  Solid = true
  Symmetric = false
FEATURE [Sketcher::SketchObject] Sketch421
  ArcFitTolerance = 0
  FullyConstrained = true
  MakeInternals = false
  Placement = pos=(0,0,-25) rot=(0,0,1;0rad)
  sketch-geometry (3):
    g0: Circle CenterX=-80 CenterY=-270.2 CenterZ=0 NormalX=0 NormalY=0 NormalZ=1 AngleXU=0 Radius=40
    g1: Circle CenterX=0 CenterY=-270.2 CenterZ=0 NormalX=0 NormalY=0 NormalZ=1 AngleXU=0 Radius=40
    g2: Circle CenterX=80 CenterY=-270.2 CenterZ=0 NormalX=0 NormalY=0 NormalZ=1 AngleXU=0 Radius=40
  constraints (9):
    c: PointOnObject(g1,g-2)
    c: Diameter(g1) = 80
    c: Diameter(g0) = 80
    c: Horizontal(g1,g0)
    c: DistanceY(g0) = -270.2
    c: DistanceX(g0) = -80
    c: Horizontal(g2,g1)
    c: Diameter(g2) = 80
    c: DistanceX(g1,g2) = 80
FEATURE [Part::Extrusion] Extrude197  label="base008"
  Base = -> Sketch421
  Dir = (0,0,1)
  DirMode = 2
  FaceMakerClass = Part::FaceMakerBullseye
  FaceMakerMode = 3
  LengthFwd = 5
  LengthRev = 0
  Solid = true
  Symmetric = false
FEATURE [Part::Fillet] Fillet265  label="base009"
  Base = -> Extrude197
  EdgeLinks = -> Extrude197 [Edge2,Edge5,Edge8]
  Edges = 3 edges r=4: [Edge2,Edge5,Edge8]
FEATURE [Sketcher::SketchObject] Sketch422
  ArcFitTolerance = 0
  FullyConstrained = true
  MakeInternals = false
  Placement = pos=(0,0,-20) rot=(0,0,1;0rad)
  sketch-geometry (2):
    g0: Circle CenterX=0 CenterY=-270 CenterZ=0 NormalX=0 NormalY=0 NormalZ=1 AngleXU=0 Radius=30
    g1: Circle CenterX=0 CenterY=-270 CenterZ=0 NormalX=0 NormalY=0 NormalZ=1 AngleXU=0 Radius=40
  constraints (5):
    c: PointOnObject(g0,g-2)
    c: Coincident(g1,g0)
    c: DistanceY(g0) = -270
    c: Diameter(g0) = 60
    c: Diameter(g1) = 80
FEATURE [Part::Extrusion] Extrude198  label="domeHolds008"
  Base = -> Sketch422
  Dir = (0,0,1)
  DirMode = 2
  FaceMakerClass = Part::FaceMakerBullseye
  FaceMakerMode = 3
  LengthFwd = 48
  LengthRev = 0
  Solid = true
  Symmetric = false
FEATURE [Sketcher::SketchObject] Sketch423
  ArcFitTolerance = 0
  FullyConstrained = true
  MakeInternals = false
  Placement = pos=(0,0,-20) rot=(0,0,1;0rad)
  sketch-geometry (2):
    g0: Circle CenterX=0 CenterY=-270 CenterZ=0 NormalX=0 NormalY=0 NormalZ=1 AngleXU=0 Radius=30
    g1: Circle CenterX=0 CenterY=-270 CenterZ=0 NormalX=0 NormalY=0 NormalZ=1 AngleXU=0 Radius=40
  constraints (5):
    c: PointOnObject(g0,g-2)
    c: Coincident(g1,g0)
    c: DistanceY(g0) = -270
    c: Diameter(g0) = 60
    c: Diameter(g1) = 80
FEATURE [Part::Extrusion] Extrude199  label="domeHolds009"
  Base = -> Sketch423
  Dir = (0,0,1)
  DirMode = 2
  FaceMakerClass = Part::FaceMakerBullseye
  FaceMakerMode = 3
  LengthFwd = 48
  LengthRev = 0
  Placement = pos=(80,0,0) rot=(0,0,1;0rad)
  Solid = true
  Symmetric = false
FEATURE [Sketcher::SketchObject] Sketch424
  ArcFitTolerance = 0
  FullyConstrained = true
  MakeInternals = false
  Placement = pos=(0,0,-20) rot=(0,0,1;0rad)
  sketch-geometry (2):
    g0: Circle CenterX=0 CenterY=-270 CenterZ=0 NormalX=0 NormalY=0 NormalZ=1 AngleXU=0 Radius=30
    g1: Circle CenterX=0 CenterY=-270 CenterZ=0 NormalX=0 NormalY=0 NormalZ=1 AngleXU=0 Radius=40
  constraints (5):
    c: PointOnObject(g0,g-2)
    c: Coincident(g1,g0)
    c: DistanceY(g0) = -270
    c: Diameter(g0) = 60
    c: Diameter(g1) = 80
FEATURE [Part::Extrusion] Extrude200  label="domeHolds010"
  Base = -> Sketch424
  Dir = (0,0,1)
  DirMode = 2
  FaceMakerClass = Part::FaceMakerBullseye
  FaceMakerMode = 3
  LengthFwd = 48
  LengthRev = 0
  Placement = pos=(-80,0,0) rot=(0,0,1;0rad)
  Solid = true
  Symmetric = false
FEATURE [Part::MultiFuse] Fusion294  label="domeHolds011"
  Shapes = -> [Extrude198,Extrude199,Extrude200]
FEATURE [Part::MultiFuse] Fusion295  label="mainLightModule015"
  Shapes = -> [Fillet265,Fillet264,Fusion294,Extrude193]
FEATURE [Part::Fillet] Fillet266  label="mainLightModule013"
  Base = -> Fusion295
  EdgeLinks = -> Fusion295 [Edge124,Edge127,Edge206,Edge218,Edge219,Edge220,Edge265,Edge268,Edge277,Edge279,Edge280,Edge281,Edge295,Edge297,Edge301,Edge302,Edge303]
  Edges = 17 edges r=4: [Edge124,Edge127,Edge206,Edge218,Edge219,Edge220,Edge265,Edge268,Edge277,Edge279,Edge280,Edge281,Edge295,Edge297,Edge301,Edge302,Edge303]
FEATURE [Part::Cut] Cut159  label="mainLightModule011"
  Base = -> Fillet266
  Tool = -> Extrude196
FEATURE [Part::MultiFuse] Fusion296  label="mainLightModule016"
  Shapes = -> [Cut159,Extrude194,Extrude195]
FEATURE [Part::Cut] Cut160  label="mainLightModule012"
  Base = -> Fusion296
  Tool = -> Fusion297
FEATURE [Part::MultiFuse] Fusion298  label="mainLightModule017"
  Shapes = -> [Extrude191,Cut160,Fillet263]
FEATURE [Part::Fillet] Fillet267
  Base = -> Fusion298
  EdgeLinks = -> Fusion298 [Edge279]
  Edges = 1 edges r=1: [Edge279]
FEATURE [Sketcher::SketchObject] Sketch
  ArcFitTolerance = 1e-06
  FullyConstrained = true
  MakeInternals = false
  sketch-geometry (2):
    g0: Circle CenterX=0 CenterY=0 CenterZ=0 NormalX=0 NormalY=0 NormalZ=1 AngleXU=0 Radius=37
    g1: Circle CenterX=0 CenterY=0 CenterZ=0 NormalX=0 NormalY=0 NormalZ=1 AngleXU=0 Radius=27
  constraints (4):
    c: Coincident(g0,g-1)
    c: Coincident(g1,g0)
    c: Diameter(g0) = 74
    c: Diameter(g1) = 54
FEATURE [Part::Extrusion] Extrude
  Base = -> Sketch
  Dir = (0,0,1)
  DirMode = 2
  FaceMakerClass = Part::FaceMakerBullseye
  FaceMakerMode = 3
  LengthFwd = 4
  LengthRev = 0
  Placement = pos=(79,-270,24) rot=(0,0,1;0rad)
  Solid = true
  Symmetric = false
